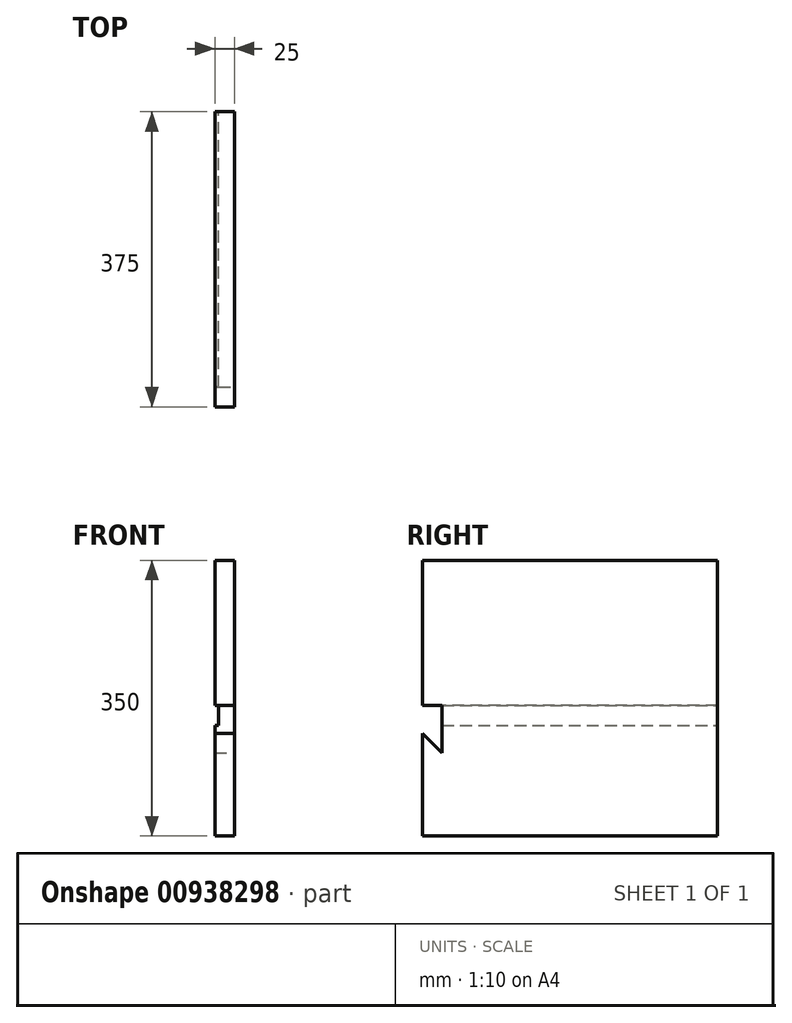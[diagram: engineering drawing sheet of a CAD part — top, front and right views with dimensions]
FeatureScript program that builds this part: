
annotation { "Feature Type Name" : "Feature", "Feature Type Description" : "" }
export const myFeature = defineFeature(function(context is Context, id is Id, definition is map)
    precondition{}
    {
        {
            var Q0;
            Q0=qCreatedBy(makeId("Front.planeOp"),FACE);
            var sketch = newSketch(context, id + "F0", { "sketchPlane" : qUnion([Q0])});
            skLineSegment(sketch, "E0.bottom", {"start": v(-69.88, 275.44) * mm, "end": v(-44.88, 275.44) * mm});
            skLineSegment(sketch, "E0.top", {"start": v(-69.88, -74.56) * mm, "end": v(-44.88, -74.56) * mm});
            skLineSegment(sketch, "E0.left", {"start": v(-69.88, 275.44) * mm, "end": v(-69.88, -74.56) * mm});
            skLineSegment(sketch, "E0.right", {"start": v(-44.88, 275.44) * mm, "end": v(-44.88, -74.56) * mm});
            skSolve(sketch);
        }
        {
            var Q0;
            Q0=makeQuery(id+"F0.imprint","IMPRINT",FACE,{"disambiguationData":[TD([[makeQuery(id+"F0.imprint","IMPRINT",EDGE,{"derivedFrom":sQuery(id+"F0.wireOp",EDGE,"E0.bottom")}),-1.0]])]});
            extrude(context, id + "F1", {"entities" : qUnion([Q0]), "depth" : 375 * mm, "offsetDistance" : 25 * mm});
        }
        {
            var Q0;
            Q0=makeQuery(id+"F1.opExtrude","SWEPT_FACE",FACE,{"disambiguationData":[OSD([sQuery(id+"F0.wireOp",EDGE,"E0.right")])]});
            var sketch = newSketch(context, id + "F2", { "sketchPlane" : qUnion([Q0])});
            skLineSegment(sketch, "E1", {"start": v(-375, 55.93) * mm, "end": v(-350, 30.93) * mm});
            skLineSegment(sketch, "E2", {"start": v(-350, 30.93) * mm, "end": v(-350, 90.93) * mm});
            skLineSegment(sketch, "E3", {"start": v(-350, 90.93) * mm, "end": v(-375, 90.93) * mm});
            skLineSegment(sketch, "E4", {"start": v(-375, 90.93) * mm, "end": v(-375, 55.93) * mm});
            skSolve(sketch);
        }
        {
            var Q0;
            Q0=makeQuery(id+"F2.imprint","IMPRINT",FACE,{"disambiguationData":[TD([[makeQuery(id+"F2.imprint","IMPRINT",EDGE,{"derivedFrom":sQuery(id+"F2.wireOp",EDGE,"E1")}),1.0]])]});
            extrude(context, id + "F3", {"entities" : qUnion([Q0]), "operationType" : NewBodyOperationType.REMOVE, "oppositeDirection" : true, "depth" : 25 * mm, "offsetDistance" : 25 * mm});
        }
        {
            var Q0;
            Q0=makeQuery(id+"F1.opExtrude","SWEPT_FACE",FACE,{"disambiguationData":[OSD([sQuery(id+"F0.wireOp",EDGE,"E0.left")])]});
            var sketch = newSketch(context, id + "F4", { "sketchPlane" : qUnion([Q0])});
            skLineSegment(sketch, "E5.bottom", {"start": v(350, 90.93) * mm, "end": v(0, 90.93) * mm});
            skLineSegment(sketch, "E5.top", {"start": v(350, 65.93) * mm, "end": v(0, 65.93) * mm});
            skLineSegment(sketch, "E5.left", {"start": v(350, 90.93) * mm, "end": v(350, 65.93) * mm});
            skLineSegment(sketch, "E5.right", {"start": v(0, 90.93) * mm, "end": v(0, 65.93) * mm});
            skSolve(sketch);
        }
        {
            var Q0;
            Q0=makeQuery(id+"F4.imprint","IMPRINT",FACE,{"disambiguationData":[TD([[makeQuery(id+"F4.imprint","IMPRINT",EDGE,{"derivedFrom":sQuery(id+"F4.wireOp",EDGE,"E5.bottom")}),1.0]])]});
            extrude(context, id + "F5", {"entities" : qUnion([Q0]), "operationType" : NewBodyOperationType.REMOVE, "oppositeDirection" : true, "depth" : 5 * mm, "offsetDistance" : 25 * mm});
        }
    });
